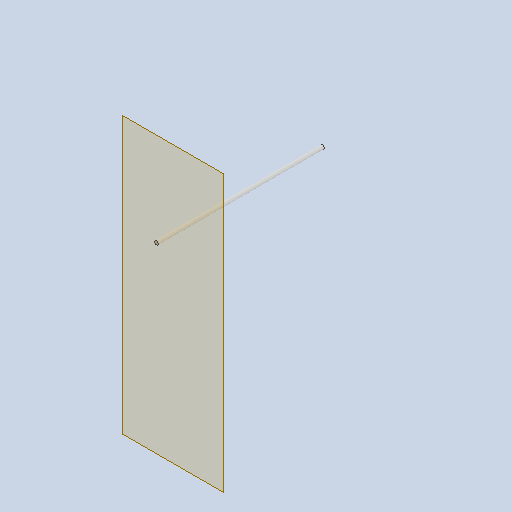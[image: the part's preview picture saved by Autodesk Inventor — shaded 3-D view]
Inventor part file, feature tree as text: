
AUTODESK INVENTOR PART (.ipt)
format: ipt  version: 2024.2 (Build 282272000, 272)  size: 119,808 bytes
history: native  units: mm
features: other x5, extrude x1, sketch x1, reference x1
ambient origin geometry x8: Origin, YZ Plane, XZ Plane, XY Plane, X Axis, Y Axis, Z Axis, Center Point
bodies: Body1 (feature_tree)
feature tree (8):
  other  "Твердое тело1"
  other  "РабПлоскость1"
  extrude  "Выдавливание1"  Depth=4.0mm
  sketch  "Эскиз1"
  reference  "Ссылка1"
  other  "<userpath>\Documents\Artist-v2\3D\Робот.iam"
  other  "Робот.iam"
  other  "бок:2"
